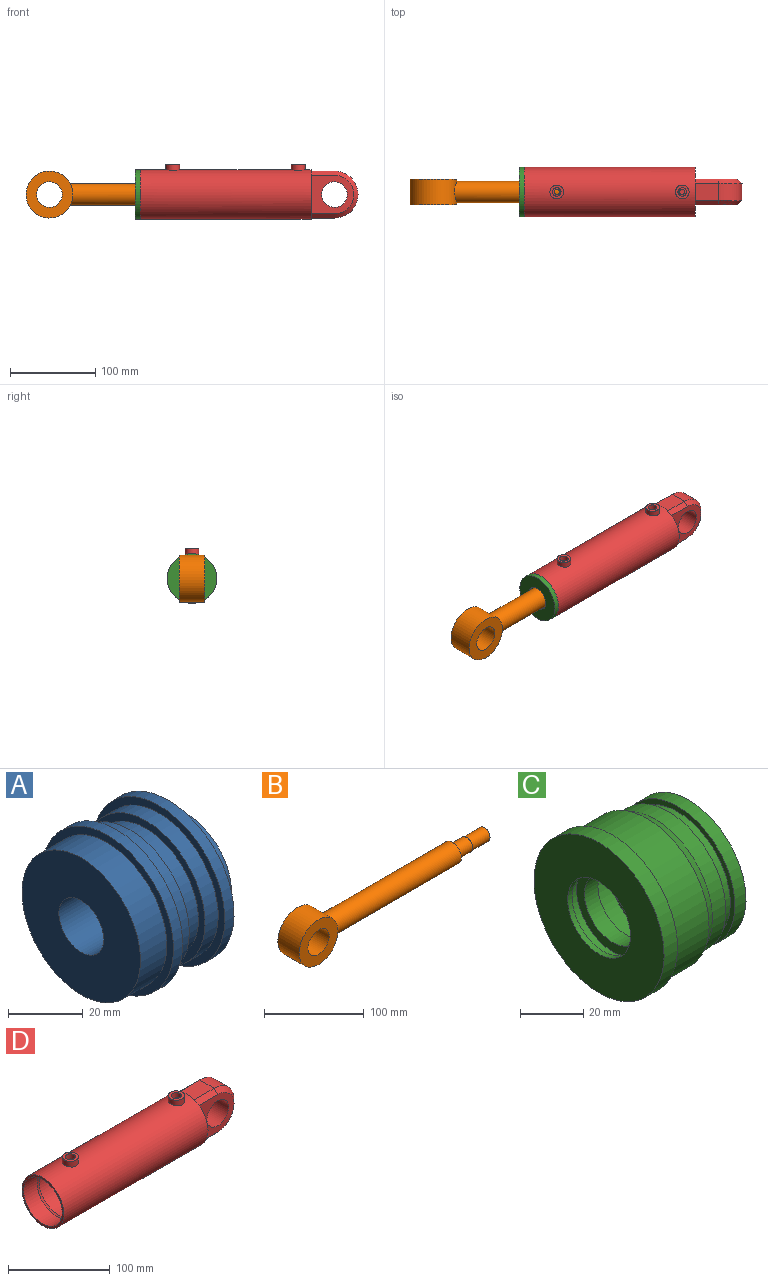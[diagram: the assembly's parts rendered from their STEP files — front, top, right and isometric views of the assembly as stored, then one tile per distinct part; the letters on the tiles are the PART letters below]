
ASSEMBLY  parts=4 mates=3
PART A: 18 faces, bbox 40x50x50 mm
  f0: plane 45x45mm, normal (-1,0,0), area 1363.5mm2, adj f1,f17
  f1: cylinder r=8.5mm len=20mm, axis (-1,0,0), area 1068.1mm2, adj f0,f2
  f2: plane 17x17mm, normal (-1,0,0), area 73mm2, adj f1,f3
  f3: cylinder r=7mm len=20mm, axis (-1,0,0), area 879.6mm2, adj f2,f4
  f4: plane 34x34mm, normal (1,0,0), area 754mm2, adj f3,f5
  f5: cylinder r=17mm len=34mm, axis (-1,0,0), area 747.7mm2, adj f4,f6
  f6: plane 50x50mm, normal (1,0,0), area 1055.6mm2, adj f5,f7
  f7: cylinder r=25mm len=50mm, axis (-1,0,0), area 549.8mm2, adj f6,f8
  f8: plane 50x50mm, normal (-1,0,0), area 373.1mm2, adj f7,f9
  f9: cylinder r=22.5mm len=45mm, axis (-1,0,0), area 706.9mm2, adj f8,f10
  f10: plane 45x45mm, normal (-1,0,0), area 333.8mm2, adj f9,f11
  f11: cylinder r=20mm len=40mm, axis (-1,0,0), area 754mm2, adj f10,f12
  f12: plane 45x45mm, normal (1,0,0), area 333.8mm2, adj f11,f13
  f13: cylinder r=22.5mm len=45mm, axis (-1,0,0), area 706.9mm2, adj f12,f14
  f14: plane 50x50mm, normal (1,0,0), area 373.1mm2, adj f13,f15
  f15: cylinder r=25mm len=50mm, axis (-1,0,0), area 549.8mm2, adj f14,f16
  f16: plane 50x50mm, normal (-1,0,0), area 373.1mm2, adj f15,f17
  f17: cylinder r=22.5mm len=45mm, axis (-1,0,0), area 1413.7mm2, adj f0,f16
PART B: 10 faces, bbox 277.5x30x55 mm
  f0: cylinder r=12.5mm len=180.51mm, axis (-1,0,0), area 14057.1mm2, adj f5,f6
  f1: plane 16x16mm, normal (1,0,0), area 201.1mm2, adj f2
  f2: cylinder r=8mm len=25mm, axis (-1,0,0), area 1256.6mm2, adj f1,f3
  f3: plane 17x17mm, normal (1,0,0), area 25.9mm2, adj f2,f4
  f4: cylinder r=8.5mm len=20mm, axis (-1,0,0), area 1068.1mm2, adj f3,f5
  f5: plane 25x25mm, normal (1,0,0), area 263.9mm2, adj f0,f4
  f6: cylinder r=27.5mm len=55mm, axis (0,1,0), area 4679mm2, adj f0,f8,f9
  f7: cylinder r=15mm len=30mm, axis (0,1,0), area 2827.4mm2, adj f8,f9
  f8: plane 55x55mm, normal (0,-1,0), area 1669mm2, adj f6,f7
  f9: plane 55x55mm, normal (0,1,0), area 1669mm2, adj f6,f7
PART C: 20 faces, bbox 40x58x58 mm
  f0: cylinder r=16mm len=32mm, axis (-1,0,0), area 402.1mm2, adj f1,f19
  f1: plane 32x32mm, normal (-1,0,0), area 313.4mm2, adj f0,f2
  f2: cylinder r=12.5mm len=25mm, axis (-1,0,0), area 471.2mm2, adj f1,f3
  f3: plane 36x36mm, normal (1,0,0), area 527mm2, adj f2,f4
  f4: cylinder r=18mm len=36mm, axis (-1,0,0), area 1131mm2, adj f3,f5
  f5: plane 36x36mm, normal (-1,0,0), area 527mm2, adj f4,f6
  f6: cylinder r=12.5mm len=25mm, axis (-1,0,0), area 1413.7mm2, adj f5,f7
  f7: plane 51x51mm, normal (1,0,0), area 1551.9mm2, adj f6,f8
  f8: cylinder r=25.5mm len=51mm, axis (-1,0,0), area 801.1mm2, adj f7,f9
  f9: plane 51x51mm, normal (-1,0,0), area 307.9mm2, adj f8,f10
  f10: cylinder r=23.5mm len=47mm, axis (-1,0,0), area 590.6mm2, adj f9,f11
  f11: plane 51x51mm, normal (1,0,0), area 307.9mm2, adj f10,f12
  f12: cylinder r=25.5mm len=51mm, axis (-1,0,0), area 961.3mm2, adj f11,f13
  f13: cone r=27.5mm half-angle=30deg, axis (-1,0,0), area 666mm2, adj f12,f14
  f14: cylinder r=27.5mm len=55mm, axis (-1,0,0), area 2684.4mm2, adj f13,f15
  f15: plane 58x58mm, normal (1,0,0), area 266.2mm2, adj f14,f16
  f16: cylinder r=29mm len=58mm, axis (-1,0,0), area 1093.3mm2, adj f15,f17
  f17: plane 58x58mm, normal (-1,0,0), area 2026.3mm2, adj f16,f18
  f18: cylinder r=14mm len=28mm, axis (-1,0,0), area 175.9mm2, adj f17,f19
  f19: plane 32x32mm, normal (1,0,0), area 188.5mm2, adj f0,f18
PART D: 38 faces, bbox 255x58x64 mm
  f0: cylinder r=25mm len=143.63mm, axis (-1,0,0), area 22532.4mm2, adj f11,f12,f37
  f1: cylinder r=29mm len=10mm, axis (-1,0,0), area 50.5mm2, adj f35,f37
  f2: cylinder r=25.5mm len=51mm, axis (-1,0,0), area 3897.2mm2, adj f10,f11,f36
  f3: cylinder r=29mm len=10mm, axis (-1,0,0), area 50.5mm2, adj f32,f36
  f4: cylinder r=29mm len=200mm, axis (-1,0,0), area 36036.9mm2, adj f5,f6,f7,f8,f13,f14,f15,f16
  f5: plane 54.11x18.55mm, normal (1,0,0), area 502.9mm2, adj f4,f23,f27,f29
  f6: plane 18.41x1.5mm, normal (1,0,0), area 18.5mm2, adj f4,f18
  f7: plane 54.11x18.55mm, normal (1,0,0), area 502.9mm2, adj f4,f22,f24,f26
  f8: plane 58x58mm, normal (-1,0,0), area 410.1mm2, adj f4,f9
  f9: cylinder r=26.65mm len=53.31mm, axis (-1,0,0), area 3098.3mm2, adj f8,f10
  f10: cone r=25.5mm half-angle=30deg, axis (-1,0,0), area 378.2mm2, adj f2,f9
  f11: cone r=25mm half-angle=20deg, axis (-1,0,0), area 231.9mm2, adj f0,f2
  f12: plane 50x50mm, normal (-1,0,0), area 1963.5mm2, adj f0
  f13: plane 18.41x1.5mm, normal (1,0,0), area 18.5mm2, adj f4,f21
  f14: plane 1.24x0.45mm, normal (-1,0,0), area 0.2mm2, adj f4,f21,f27
  f15: plane 1.24x0.45mm, normal (-1,0,0), area 0.2mm2, adj f4,f18,f29
  f16: plane 1.24x0.45mm, normal (-1,0,0), area 0.2mm2, adj f4,f18,f26
  f17: plane 1.24x0.45mm, normal (-1,0,0), area 0.2mm2, adj f4,f21,f24
  f18: plane 27.5x20mm, normal (0,0,-1), area 550mm2, adj f6,f15,f16,f19,f26,f29
  f19: cylinder r=27.5mm len=55mm, axis (0,1,0), area 1727.9mm2, adj f18,f21,f25,f28
  f20: cylinder r=15mm len=30mm, axis (0,1,0), area 2827.4mm2, adj f22,f23
  f21: plane 27.5x20mm, normal (0,0,1), area 550mm2, adj f13,f14,f17,f19,f24,f27
  f22: plane 50x45mm, normal (0,-1,0), area 1325.9mm2, adj f7,f20,f24,f25,f26
  f23: plane 50x45mm, normal (0,1,0), area 1325.9mm2, adj f5,f20,f27,f28,f29
  f24: plane 27.5x5mm, normal (0,-0.71,0.71), area 194.5mm2, adj f7,f17,f21,f22,f25
  f25: cone r=22.5mm half-angle=45deg, axis (0,1,0), area 555.4mm2, adj f19,f22,f24,f26
  f26: plane 27.5x5mm, normal (0,-0.71,-0.71), area 194.5mm2, adj f7,f16,f18,f22,f25
  f27: plane 27.5x5mm, normal (0,0.71,0.71), area 194.5mm2, adj f5,f14,f21,f23,f28
  f28: cone r=27.5mm half-angle=45deg, axis (0,-1,0), area 555.4mm2, adj f19,f23,f27,f29
  f29: plane 27.5x5mm, normal (0,0.71,-0.71), area 194.5mm2, adj f5,f15,f18,f23,f28
  f30: plane 16x16mm, normal (0,0,1), area 122.5mm2, adj f31,f32
  f31: cylinder r=8mm len=16mm, axis (0,0,1), area 329.7mm2, adj f4,f30
  f32: cylinder r=5mm len=10mm, axis (0,0,1), area 195.3mm2, adj f3,f30
  f33: plane 16x16mm, normal (0,0,1), area 122.5mm2, adj f34,f35
  f34: cylinder r=8mm len=16mm, axis (0,0,1), area 329.7mm2, adj f4,f33
  f35: cylinder r=5mm len=10mm, axis (0,0,1), area 195.3mm2, adj f1,f33
  f36: cylinder r=3mm len=6mm, axis (0,0,1), area 66.2mm2, adj f2,f3
  f37: cylinder r=3mm len=6mm, axis (0,0,1), area 75.6mm2, adj f0,f1
PLACE A t=(-27.08,27.26,-64.48)mm
PLACE B t=(-27.08,27.26,-64.48)mm
PLACE C rot(axis=(-0.51,-0.42,-0.75),0deg) t=(18.65,27.26,-64.48)mm
PLACE D rot(axis=(-0.51,-0.42,-0.75),0deg) t=(18.65,27.26,-64.48)mm fixed
MATE fastened C.f0 <-> D.f0  axis (1,0,0) through (79.35,27.26,-64.48)mm
MATE cylindrical B.f0 <-> D.f0  axis (-1,0,0) through (87.11,27.26,-64.48)mm
MATE fastened A.f1 <-> B.f0  axis (-1,0,0) through (177.92,27.26,-64.48)mm
